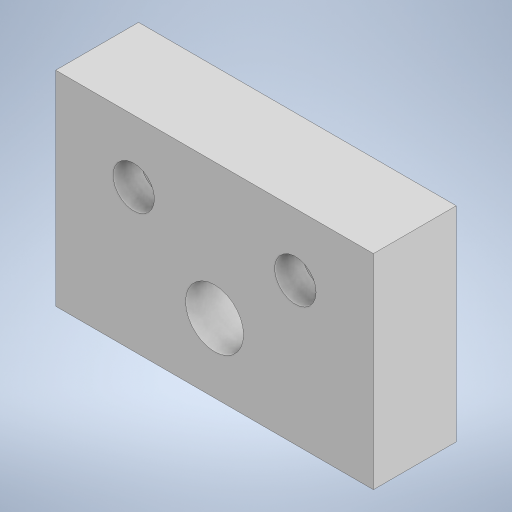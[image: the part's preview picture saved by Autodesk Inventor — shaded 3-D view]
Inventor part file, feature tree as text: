
AUTODESK INVENTOR PART (.ipt)
format: ipt  version: 2023.5 (Build 275446000, 446)  size: 215,552 bytes
history: native  units: in
note: dims shown in document units (in); Inventor stores cm internally (conversion verified against a paired STEP export)
features: extrude x2
ambient origin geometry x8: Origin, YZ Plane, XZ Plane, XY Plane, X Axis, Y Axis, Z Axis, Center Point
bodies: Solid1 (feature_tree)
feature tree (2):
  extrude  "Extrusion1"  Depth=0.9055in
  extrude  "Extrusion2"  Depth=0.5827in
